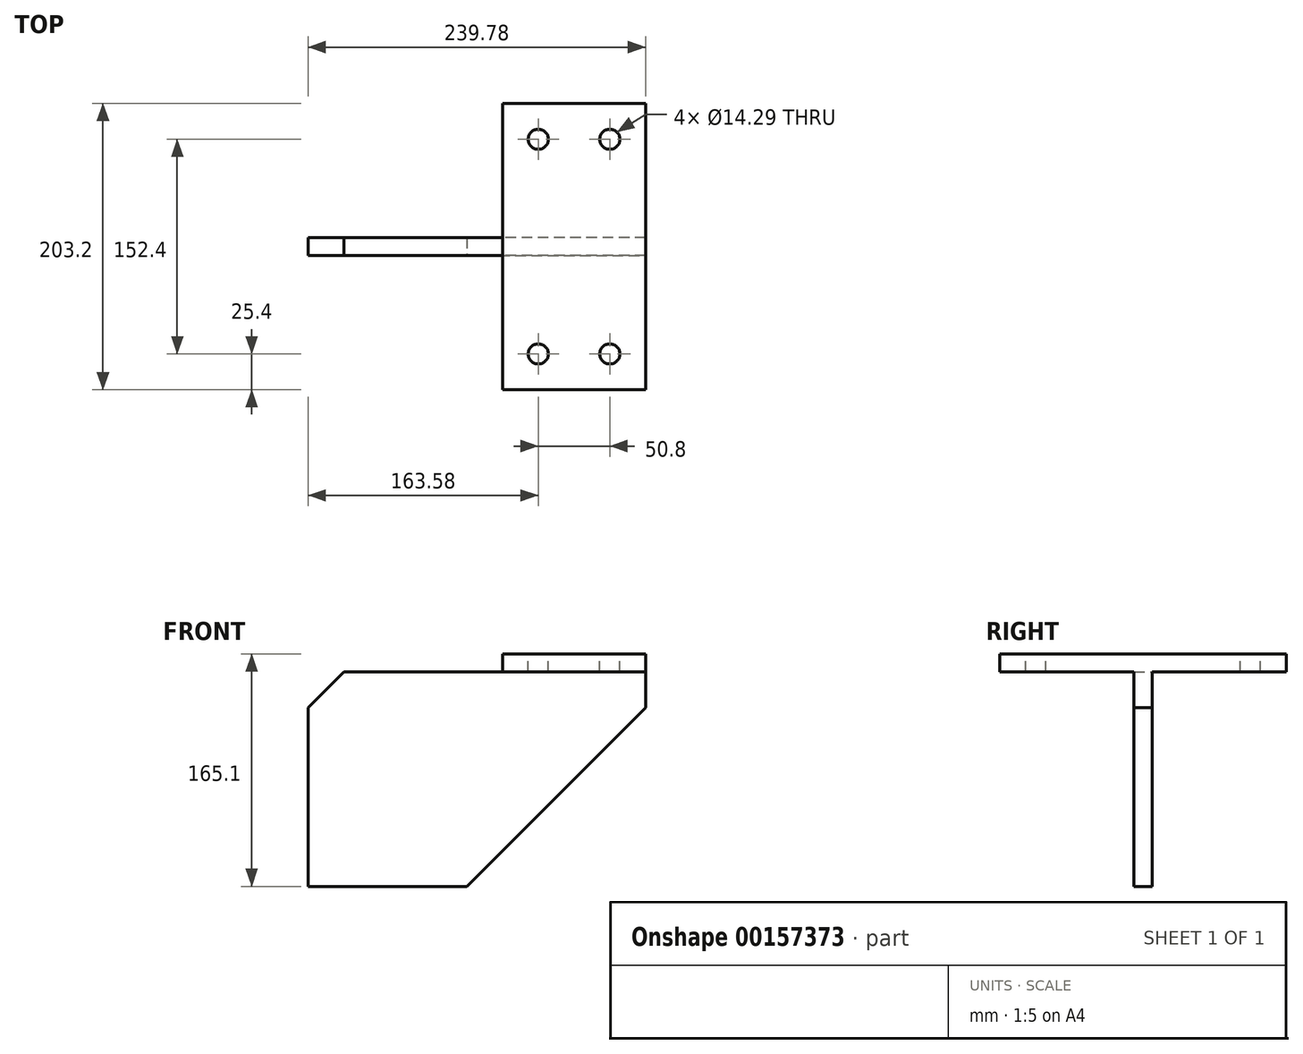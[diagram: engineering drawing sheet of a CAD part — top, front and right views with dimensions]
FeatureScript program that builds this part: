
annotation { "Feature Type Name" : "Feature", "Feature Type Description" : "" }
export const myFeature = defineFeature(function(context is Context, id is Id, definition is map)
    precondition{}
    {
        {
            var Q0;
            Q0=qCreatedBy(makeId("Front.planeOp"),FACE);
            var sketch = newSketch(context, id + "F0", { "sketchPlane" : qUnion([Q0])});
            skLineSegment(sketch, "E0.bottom", {"start": v(0, 0) * mm, "end": v(101.6, 0) * mm});
            skLineSegment(sketch, "E0.top", {"start": v(0, 12.7) * mm, "end": v(101.6, 12.7) * mm});
            skLineSegment(sketch, "E0.left", {"start": v(0, 0) * mm, "end": v(0, 12.7) * mm});
            skLineSegment(sketch, "E0.right", {"start": v(101.6, 0) * mm, "end": v(101.6, 12.7) * mm});
            skSolve(sketch);
        }
        {
            var Q0;
            Q0=qSketchRegion(id+"F0",true);
            extrude(context, id + "F1", {"entities" : qUnion([Q0]), "endBound" : BoundingType.SYMMETRIC, "depth" : 203.2 * mm});
        }
        {
            var Q0;
            Q0=makeQuery(id+"F1.opExtrude","SWEPT_FACE",FACE,{"disambiguationData":[OSD([sQuery(id+"F0.wireOp",EDGE,"E0.top")])]});
            var sketch = newSketch(context, id + "F2", { "sketchPlane" : qUnion([Q0])});
            skLineSegment(sketch, "E1", {"start": v(101.6, 0) * mm, "end": v(0, 0) * mm, "construction": true});
            skLineSegment(sketch, "E2", {"start": v(50.8, 101.6) * mm, "end": v(50.8, -101.6) * mm, "construction": true});
            skLineSegment(sketch, "E3.0", {"start": v(25.4, 101.6) * mm, "end": v(25.4, -101.6) * mm, "construction": true});
            skLineSegment(sketch, "E4.0", {"start": v(101.6, -76.2) * mm, "end": v(0, -76.2) * mm, "construction": true});
            skPoint(sketch, "E5", {"position": v(25.4, -76.2) * mm});
            skPoint(sketch, "E6.MirrorP", {"position": v(76.2, -76.2) * mm});
            skPoint(sketch, "E7.MirrorP", {"position": v(25.4, 76.2) * mm});
            skPoint(sketch, "E8.MirrorP", {"position": v(76.2, 76.2) * mm});
            skSolve(sketch);
        }
        {
            var Q0;
            Q0=sQuery(id+"F2.wireOp",VERTEX,"E5");
            var Q1;
            Q1=sQuery(id+"F2.wireOp",VERTEX,"E6.MirrorP");
            var Q2;
            Q2=sQuery(id+"F2.wireOp",VERTEX,"E8.MirrorP");
            var Q3;
            Q3=sQuery(id+"F2.wireOp",VERTEX,"E7.MirrorP");
            var Q4;
            Q4=makeQuery(id+"F1.opExtrude","SWEPT_BODY",BODY,{"disambiguationData":[OSD([sQuery(id+"F0.wireOp",EDGE,"E0.bottom"),sQuery(id+"F0.wireOp",EDGE,"E0.top"),sQuery(id+"F0.wireOp",EDGE,"E0.left"),sQuery(id+"F0.wireOp",EDGE,"E0.right")])]});
            hole(context, id + "F3", {"style" : HoleStyle.SIMPLE, "holeDiameter" : 14.29 * mm, "endStyle" : HoleEndStyle.THROUGH, "locations" : qUnion([Q0, Q1, Q2, Q3]), "scope" : qUnion([Q4])});
        }
        {
            var Q0;
            Q0=qCreatedBy(makeId("Front.planeOp"),FACE);
            var sketch = newSketch(context, id + "F4", { "sketchPlane" : qUnion([Q0])});
            skLineSegment(sketch, "E9.0", {"start": v(0, 0) * mm, "end": v(101.6, 0) * mm, "construction": true});
            skLineSegment(sketch, "E10.bottom", {"start": v(101.6, 0) * mm, "end": v(-138.18, 0) * mm});
            skLineSegment(sketch, "E10.top", {"start": v(101.6, -152.4) * mm, "end": v(-138.18, -152.4) * mm});
            skLineSegment(sketch, "E10.left", {"start": v(101.6, 0) * mm, "end": v(101.6, -152.4) * mm});
            skLineSegment(sketch, "E10.right", {"start": v(-138.18, 0) * mm, "end": v(-138.18, -152.4) * mm});
            skSolve(sketch);
        }
        {
            var Q0;
            Q0=qSketchRegion(id+"F4",true);
            extrude(context, id + "F5", {"entities" : qUnion([Q0]), "operationType" : NewBodyOperationType.ADD, "endBound" : BoundingType.SYMMETRIC, "depth" : 12.7 * mm});
        }
        {
            var Q0;
            Q0=makeQuery(id+"F5.opExtrude","SWEPT_EDGE",EDGE,{"disambiguationData":[OSD([sQuery(id+"F4.wireOp",EDGE,"E10.bottom"),sQuery(id+"F4.wireOp",EDGE,"E10.right")])]});
            chamfer(context, id + "F6", {"entities" : qUnion([Q0]), "width" : 25.4 * mm, "tangentPropagation" : true});
        }
        {
            var Q0;
            Q0=makeQuery(id+"F5.opExtrude","SWEPT_EDGE",EDGE,{"disambiguationData":[OSD([sQuery(id+"F4.wireOp",EDGE,"E10.top"),sQuery(id+"F4.wireOp",EDGE,"E10.left")])]});
            chamfer(context, id + "F7", {"entities" : qUnion([Q0]), "width" : 127 * mm, "tangentPropagation" : true});
        }
    });
